# Revit family: EL_Teko_Flex
name_source: partatom
category: Lighting Fixtures
units: mm (PartAtom-declared; Revit-internal decimal feet)

## family parameters
Always vertical = Yes
Cut with Voids When Loaded = No
Light Source = Yes
Maintain Annotation Orientation = No
OmniClass Number = 23.80.70.00
OmniClass Title = Lighting
Part Type = Normal
Room Calculation Point = No
Round Connector Dimension = Use Diameter
Shared = No
Work Plane-Based = No

## types (39) — shared parameters
CE Conformity = CE Mark
Certification = ENEC, ENEC+, EMC, Zhaga D4i, IDA
Color Filter = 16777215
Control Gear = LED Driver
Default Elevation = 1500 mm  [stored 4.92126 ft]
Description = Street luminaire
Diffuser Material  = Flat glass
Dimming Lamp Color Temperature Shift = <None>
EL_Voltage = AC 220V - 240V / 50-60Hz
Emit from Line Length = 610 mm
Housing Height = 113 mm  [stored 0.370735 ft]
Housing Length = 490 mm  [stored 1.60761 ft]
Housing Width = 440 mm  [stored 1.44357 ft]
IK = IK 09 / IK10
IP = IP66
Lamp = LED
Life Time = 120 000 h
Light Source Symbol Length = 3048 mm  [stored 10 ft]
Luminaire Material = Kov
Luminaire Type = TEKO F(lex)
Manufacturer = ELEKTRO-LUMEN, s. r. o.
Model = TEKO F(lex)
Spot Beam Angle = 30.00°
Spot Field Angle = 90.00°
Terminal Block Poles = 2, 3, 5
Tilt Angle = 90.00°
URL Luminaire = https://www.el-lumen.cz
URL Manufacturer = https://www.el-lumen.cz
Voltage  = AC 220V - 240V / 50-60Hz
Weight = 9.2

## per-type parameters (varying)
| type | CCT | CRI | Luminous Flux of LED | Luminous Flux of Luminaire | Optic | Optical Efficacy | Power |
| TEKO F(lex)  Mxx 10k0 740 | 4000 | 70 | 10000 lm | 8120 lm | M03 | 81.2 | 59 W |
| TEKO F(lex)  Mxx 9k0 740 | 4000 | 70 | 9000 lm | 7308 lm | M03 | 81.2 | 52 W |
| TEKO F(lex)  Mxx 8k0 740 | 4000 | 70 | 8000 lm | 6496 lm | M03 | 81.2 | 45 W |
| TEKO F(lex)  Mxx 7k0 740 | 4000 | 70 | 7000 lm | 5684 lm | M03 | 81.2 | 39 W |
| TEKO F(lex)  Mxx 6k0 740 | 4000 | 70 | 6000 lm | 4872 lm | M03 | 81.2 | 37 W |
| TEKO F(lex)  Mxx 5k0 740 | 4000 | 70 | 5000 lm | 4060 lm | M03 | 81.2 | 31 W |
| TEKO F(lex)  Mxx 4k0 740 | 4000 | 70 | 4000 lm | 3248 lm | M03 | 81.2 | 24 W |
| TEKO F(lex)  Mxx 3k0 740 | 4000 | 70 | 3000 lm | 2436 lm | M03 | 81.2 | 18 W |
| TEKO F(lex)  Mxx 2k0 740 | 4000 | 70 | 2000 lm | 1624 lm | M03 | 81.2 | 12 W |
| TEKO F(lex)  Mxx 9k0 730 | 3000 | 70 | 9000 lm | 7308 lm | M03 | 81.2 | 55 W |
| TEKO F(lex)  Mxx 8k0 730 | 3000 | 70 | 8000 lm | 6496 lm | M03 | 81.2 | 48 W |
| TEKO F(lex)  Mxx 7k0 730 | 3000 | 70 | 7000 lm | 5684 lm | M03 | 81.2 | 42 W |
| TEKO F(lex)  Mxx 6k0 730 | 3000 | 70 | 6000 lm | 4872 lm | M03 | 81.2 | 40 W |
| TEKO F(lex)  Mxx 5k0 730 | 3000 | 70 | 5000 lm | 4060 lm | M03 | 81.2 | 32 W |
| TEKO F(lex)  Mxx 4k0 730 | 3000 | 70 | 4000 lm | 3248 lm | M03 | 81.2 | 25 W |
| TEKO F(lex)  Mxx 3k0 730 | 3000 | 70 | 3000 lm | 2436 lm | M03 | 81.2 | 18 W |
| TEKO F(lex)  Mxx 2k0 730 | 3000 | 70 | 2000 lm | 1624 lm | M03 | 81.2 | 12 W |
| TEKO F(lex)  Mxx 9k0 727 | 2700 | 70 | 9000 lm | 7308 lm | M03 | 81.2 | 59 W |
| TEKO F(lex)  Mxx 8k0 727 | 2700 | 70 | 8000 lm | 6496 lm | M03 | 81.2 | 51 W |
| TEKO F(lex)  Mxx 7k0 727 | 2700 | 70 | 7000 lm | 5684 lm | M03 | 81.2 | 44 W |
| TEKO F(lex)  Mxx 6k0 727 | 2700 | 70 | 6000 lm | 4872 lm | M03 | 81.2 | 43 W |
| TEKO F(lex)  Mxx 5k0 727 | 2700 | 70 | 5000 lm | 4060 lm | M03 | 81.2 | 34 W |
| TEKO F(lex)  Mxx 4k0 727 | 2700 | 70 | 4000 lm | 3248 lm | M03 | 81.2 | 27 W |
| TEKO F(lex)  Mxx 3k0 727 | 2700 | 70 | 3000 lm | 2436 lm | M03 | 81.2 | 20 W |
| TEKO F(lex)  Mxx 2k0 727 | 2700 | 70 | 2000 lm | 1624 lm | M03 | 81.2 | 13 W |
| TEKO F(lex)  Mxx 8k0 722 | 2200 | 70 | 8000 lm | 6496 lm | M03 | 81.2 | 60 W |
| TEKO F(lex)  Mxx 7k0 722 | 2200 | 70 | 7000 lm | 5684 lm | M03 | 81.2 | 51 W |
| TEKO F(lex)  Mxx 6k0 722 | 2200 | 70 | 6000 lm | 4872 lm | M03 | 81.2 | 43 W |
| TEKO F(lex)  Mxx 5k0 722 | 2200 | 70 | 5000 lm | 4060 lm | M03 | 81.2 | 40 W |
| TEKO F(lex)  Mxx 4k0 722 | 2200 | 70 | 4000 lm | 3248 lm | M03 | 81.2 | 31 W |
| TEKO F(lex)  Mxx 3k0 722 | 2200 | 70 | 3000 lm | 2436 lm | M03 | 81.2 | 23 W |
| TEKO F(lex)  Mxx 2k0 722 | 2200 | 70 | 2000 lm | 1624 lm | M03 | 81.2 | 15 W |
| TEKO F(lex)  Lxx 8k0 AMB | 1850 | 50 | 8000 lm | 6364 lm | L03 | 79.55 | 54 W |
| TEKO F(lex)  Lxx 7K0 AMB | 1850 | 50 | 7000 lm | 5569 lm | L03 | 79.55 | 47 W |
| TEKO F(lex)  Lxx 6k0 AMB | 1850 | 50 | 6000 lm | 4773 lm | L03 | 79.55 | 40 W |
| TEKO F(lex)  Lxx 5k0 AMB | 1850 | 50 | 5000 lm | 3978 lm | L03 | 79.55 | 36 W |
| TEKO F(lex)  Lxx 4k0 AMB | 1850 | 50 | 4000 lm | 3182 lm | L03 | 79.55 | 28 W |
| TEKO F(lex)  Lxx 3k0 AMB | 1850 | 50 | 3000 lm | 2387 lm | L03 | 79.55 | 21 W |
| TEKO F(lex)  Lxx 2k0 AMB | 1850 | 50 | 2000 lm | 1591 lm | L03 | 79.55 | 14 W |

note: column(s) folded — value = type name in every type: Luminaire Model

note: [stored X ft] marks values corroborated as IEEE doubles in the binary element streams (Revit-internal decimal feet)
